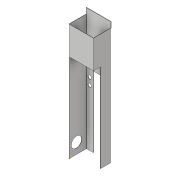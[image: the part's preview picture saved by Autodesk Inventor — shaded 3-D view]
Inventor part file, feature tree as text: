
AUTODESK INVENTOR PART (.ipt)
format: ipt  version: 2019 (Build 230136000, 136)  size: 255,488 bytes
history: native  units: mm
features: sketch x22, sheet_metal_op x21, other x8, extrude x7
ambient origin geometry x8: Origin, YZ Plane, XZ Plane, XY Plane, X Axis, Y Axis, Z Axis, Center Point
bodies: Solid1 (feature_tree)
feature tree (58):
  sheet_metal_op  "Face1"
  sheet_metal_op  "Flange1"
  sheet_metal_op  "Flange2"
  sheet_metal_op  "Flange3"
  sketch  "Sketch5"  dims[d12=0.5mm d13=0.5mm]
  sketch  "Sketch6"  dims[d14=0.25mm d15=1.0mm]
  extrude  "Extrusion1"  Depth=0.5mm
  sketch  "Sketch8"  dims[d20=2.0mm]
  sheet_metal_op  "Flange4"
  sheet_metal_op  "Flange5"
  sheet_metal_op  "Flange6"
  extrude  "Extrusion2"  Depth=1.0mm
  extrude  "Extrusion3"  Depth=25.0mm TaperAngle=90.0deg
  extrude  "Extrusion4"  Depth=0.5mm
  extrude  "Extrusion5"  Depth=0.5mm
  extrude  "Extrusion6"  Depth=1.0mm
  sketch  "Sketch17"  dims[d31=0.5mm]
  sketch  "Sketch18"  dims[d32=0.5mm]
  sketch  "Sketch19"  dims[d33=30.0mm]
  sheet_metal_op  "Face2"
  sketch  "Sketch21"  dims[d35=10.0mm d36=0.0mm]
  extrude  "Extrusion7"  Depth=25.0mm TaperAngle=90.0deg
  sketch  "Sketch1"  dims[d2=0.5mm d3=0.5mm]
  other  "Plate1"
  sketch  "Sketch2"  dims[d4=0.25mm d5=1.0mm]
  other  "Plate2"
  sheet_metal_op  "Bend1"
  sheet_metal_op  "Corner1"
  sketch  "Sketch3"  dims[d6=0.5mm d7=25.0mm d8=90.0deg d9=0.5mm]
  other  "Plate3"
  sheet_metal_op  "Bend2"
  sheet_metal_op  "Corner2"
  sketch  "Sketch4"  dims[d10=2.0mm d11=0.5mm]
  other  "Plate4"
  sheet_metal_op  "Bend3"
  sheet_metal_op  "Corner3"
  sketch  "Sketch7"  dims[d16=0.5mm d17=25.0mm d18=90.0deg d19=0.5mm]
  sketch  "Sketch9"  dims[d21=0.5mm]
  other  "Plate5"
  sheet_metal_op  "Bend4"
  sheet_metal_op  "Corner4"
  sketch  "Sketch10"  dims[d22=0.5mm]
  other  "Plate6"
  sheet_metal_op  "Bend5"
  sheet_metal_op  "Corner5"
  sketch  "Sketch11"  dims[d23=0.5mm]
  other  "Plate7"
  sheet_metal_op  "Bend6"
  sheet_metal_op  "Corner6"
  sketch  "Sketch12"  dims[d24=0.25mm]
  sketch  "Sketch13"  dims[d25=1.0mm]
  sketch  "Sketch14"  dims[d26=0.5mm]
  sketch  "Sketch15"  dims[d27=32.0mm d28=90.0deg d29=0.5mm]
  sketch  "Sketch16"  dims[d30=2.0mm]
  sketch  "Sketch20"  dims[d34=125.0mm]
  other  "Plate8"
  sheet_metal_op  "Bend7"
  sketch  "Sketch22"  dims[d37=35.0mm d38=0.5mm d39=0.25mm d40=1.0mm d41=0.5mm d42=25.0mm d43=90.0deg d44=0.5mm d45=2.0mm d46=0.5mm d47=0.5mm d48=0.5mm d49=0.25mm d50=1.0mm d51=0.5mm d52=25.0mm d53=90.0deg d54=0.5mm d55=2.0mm d56=0.5mm d57=0.5mm d58=0.5mm d59=0.25mm d60=1.0mm d61=0.5mm d62=35.0mm d63=90.0deg d64=0.5mm d65=2.0mm d66=0.5mm d67=0.5mm d68=34.0mm d69=125.0mm d70=10.0mm d71=0.0mm d72=10.0mm d73=10.0mm d74=15.0mm d75=10.0mm d76=10.0mm d77=0.0mm d78=10.0mm d79=15.0mm d80=90.0deg d81=15.0mm d82=10.0mm d83=0.0mm d84=5.0mm d85=10.0mm d86=10.0mm d87=50.0mm d88=10.0mm d89=10.0mm d90=5.0mm d91=10.0mm d92=10.0mm d93=50.0mm d94=10.0mm d95=10.0mm d96=10.0mm d97=10.0mm d100=5.0mm d101=5.0mm d102=5.0mm d103=5.0mm d104=5.0mm d105=5.0mm d108=10.0mm d109=0.0mm d110=5.0mm d111=80.0mm d112=10.0mm d113=10.0mm d114=5.0mm d115=5.0mm d116=5.0mm d117=5.0mm d118=0.0mm d119=0.0mm d120=35.0mm d121=15.0mm d122=35.0mm d123=15.0mm d124=0.5mm d125=0.5mm d126=0.25mm d127=1.0mm d128=0.5mm d129=10.0mm d130=0.0mm]
